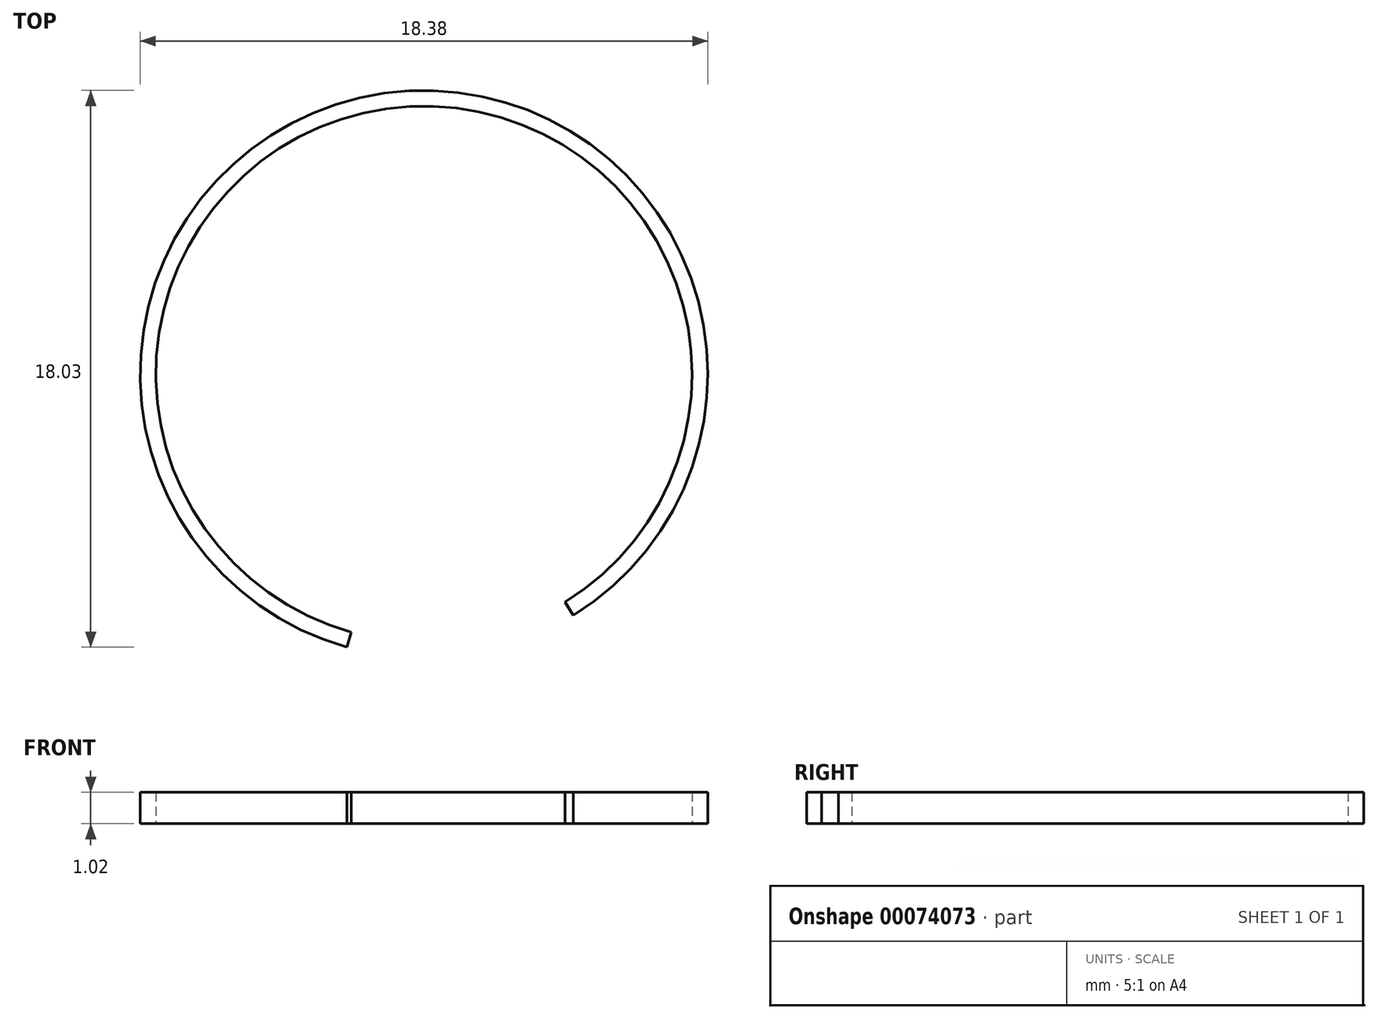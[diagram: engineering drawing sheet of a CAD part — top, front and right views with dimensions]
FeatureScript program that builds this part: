
annotation { "Feature Type Name" : "Feature", "Feature Type Description" : "" }
export const myFeature = defineFeature(function(context is Context, id is Id, definition is map)
    precondition{}
    {
        {
            var Q0;
            Q0=qCreatedBy(makeId("Top.planeOp"),FACE);
            var sketch = newSketch(context, id + "F1", { "sketchPlane" : qUnion([Q0])});
            skArc(sketch, "E0", {"start": v(4.84, -7.81) * mm, "mid": v(-1.28, 9.1) * mm, "end": v(-2.5, -8.84) * mm});
            skArc(sketch, "E1", {"start": v(4.57, -7.38) * mm, "mid": v(-1.21, 8.6) * mm, "end": v(-2.35, -8.36) * mm});
            skLineSegment(sketch, "E2", {"start": v(-2.35, -8.36) * mm, "end": v(-2.5, -8.84) * mm});
            skLineSegment(sketch, "E3", {"start": v(4.57, -7.38) * mm, "end": v(4.84, -7.81) * mm});
            skSolve(sketch);
        }
        {
            var Q0;
            Q0=makeQuery(id+"F1.imprint","IMPRINT",FACE,{"disambiguationData":[TD([[makeQuery(id+"F1.imprint","IMPRINT",EDGE,{"derivedFrom":sQuery(id+"F1.wireOp",EDGE,"E0")}),1.0]])]});
            extrude(context, id + "F0", {"entities" : qUnion([Q0]), "depth" : 1.02 * mm});
        }
    });
